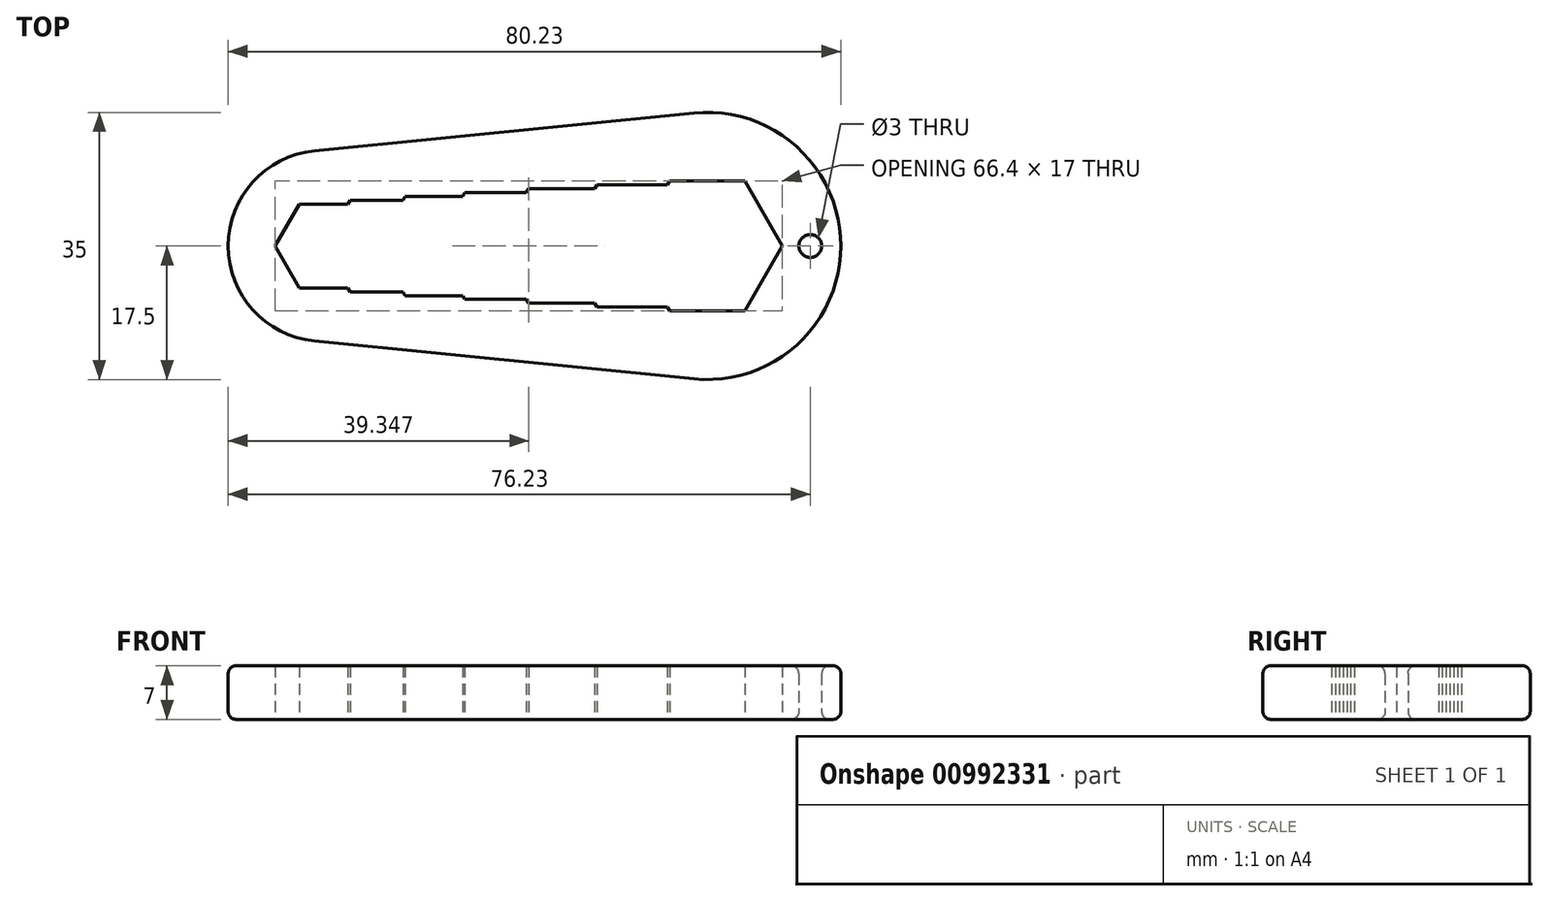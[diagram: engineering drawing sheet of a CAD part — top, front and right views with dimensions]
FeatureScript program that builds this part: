
annotation { "Feature Type Name" : "Feature", "Feature Type Description" : "" }
export const myFeature = defineFeature(function(context is Context, id is Id, definition is map)
    precondition{}
    {
        {
            var Q0;
            Q0=qCreatedBy(makeId("Top.planeOp"),FACE);
            var sketch = newSketch(context, id + "F0", { "sketchPlane" : qUnion([Q0])});
            skArc(sketch, "E0", {"start": v(-1.74, -17.41) * mm, "mid": v(17.5, 0) * mm, "end": v(-1.74, 17.41) * mm});
            skArc(sketch, "E1", {"start": v(-51.47, 12.44) * mm, "mid": v(-62.73, 0) * mm, "end": v(-51.47, -12.44) * mm});
            skLineSegment(sketch, "E2", {"start": v(-51.47, 12.44) * mm, "end": v(-1.74, 17.41) * mm});
            skLineSegment(sketch, "E3", {"start": v(-51.47, -12.44) * mm, "end": v(-1.74, -17.41) * mm});
            skCircle(sketch, "E4.cCircle", {"center": v(0, 0) * mm, "radius": 8.5 * mm, "construction": true});
            skLineSegment(sketch, "E4.0", {"start": v(9.81, 0) * mm, "end": v(4.9, -8.5) * mm});
            skLineSegment(sketch, "E4.1", {"start": v(4.9, -8.5) * mm, "end": v(-4.9, -8.5) * mm});
            skLineSegment(sketch, "E4.2", {"start": v(-4.9, -8.5) * mm, "end": v(-9.81, 0) * mm});
            skLineSegment(sketch, "E4.3", {"start": v(-9.81, 0) * mm, "end": v(-4.9, 8.5) * mm});
            skLineSegment(sketch, "E4.4", {"start": v(-4.9, 8.5) * mm, "end": v(4.9, 8.5) * mm});
            skLineSegment(sketch, "E4.5", {"start": v(4.9, 8.5) * mm, "end": v(9.81, 0) * mm});
            skPoint(sketch, "E4.0.midPoint", {"position": v(7.36, -4.25) * mm});
            skCircle(sketch, "E5.cCircle", {"center": v(-9.81, 0) * mm, "radius": 8 * mm, "construction": true});
            skLineSegment(sketch, "E5.0", {"start": v(-0.58, 0) * mm, "end": v(-5.2, -8) * mm});
            skLineSegment(sketch, "E5.1", {"start": v(-5.2, -8) * mm, "end": v(-14.43, -8) * mm});
            skLineSegment(sketch, "E5.2", {"start": v(-14.43, -8) * mm, "end": v(-19.05, 0) * mm});
            skLineSegment(sketch, "E5.3", {"start": v(-19.05, 0) * mm, "end": v(-14.43, 8) * mm});
            skLineSegment(sketch, "E5.4", {"start": v(-14.43, 8) * mm, "end": v(-5.2, 8) * mm});
            skLineSegment(sketch, "E5.5", {"start": v(-5.2, 8) * mm, "end": v(-0.58, 0) * mm});
            skPoint(sketch, "E5.0.midPoint", {"position": v(-2.89, -4) * mm});
            skCircle(sketch, "E6.cCircle", {"center": v(-19.05, 0) * mm, "radius": 7.5 * mm, "construction": true});
            skLineSegment(sketch, "E6.0", {"start": v(-10.4, 0) * mm, "end": v(-14.72, -7.5) * mm});
            skLineSegment(sketch, "E6.1", {"start": v(-14.72, -7.5) * mm, "end": v(-23.38, -7.5) * mm});
            skLineSegment(sketch, "E6.2", {"start": v(-23.38, -7.5) * mm, "end": v(-27.71, 0) * mm});
            skLineSegment(sketch, "E6.3", {"start": v(-27.71, 0) * mm, "end": v(-23.38, 7.5) * mm});
            skLineSegment(sketch, "E6.4", {"start": v(-23.38, 7.5) * mm, "end": v(-14.72, 7.5) * mm});
            skLineSegment(sketch, "E6.5", {"start": v(-14.72, 7.5) * mm, "end": v(-10.4, 0) * mm});
            skPoint(sketch, "E6.0.midPoint", {"position": v(-12.56, -3.75) * mm});
            skCircle(sketch, "E7.cCircle", {"center": v(-27.71, 0) * mm, "radius": 7 * mm, "construction": true});
            skLineSegment(sketch, "E7.0", {"start": v(-19.63, 0) * mm, "end": v(-23.67, -7) * mm});
            skLineSegment(sketch, "E7.1", {"start": v(-23.67, -7) * mm, "end": v(-31.75, -7) * mm});
            skLineSegment(sketch, "E7.2", {"start": v(-31.75, -7) * mm, "end": v(-35.8, 0) * mm});
            skLineSegment(sketch, "E7.3", {"start": v(-35.8, 0) * mm, "end": v(-31.75, 7) * mm});
            skLineSegment(sketch, "E7.4", {"start": v(-31.75, 7) * mm, "end": v(-23.67, 7) * mm});
            skLineSegment(sketch, "E7.5", {"start": v(-23.67, 7) * mm, "end": v(-19.63, 0) * mm});
            skPoint(sketch, "E7.0.midPoint", {"position": v(-21.65, -3.5) * mm});
            skCircle(sketch, "E8.cCircle", {"center": v(-35.8, 0) * mm, "radius": 6.5 * mm, "construction": true});
            skLineSegment(sketch, "E8.0", {"start": v(-28.3, 0) * mm, "end": v(-32.04, -6.5) * mm});
            skLineSegment(sketch, "E8.1", {"start": v(-32.04, -6.5) * mm, "end": v(-39.55, -6.5) * mm});
            skLineSegment(sketch, "E8.2", {"start": v(-39.55, -6.5) * mm, "end": v(-43.3, 0) * mm});
            skLineSegment(sketch, "E8.3", {"start": v(-43.3, 0) * mm, "end": v(-39.55, 6.5) * mm});
            skLineSegment(sketch, "E8.4", {"start": v(-39.55, 6.5) * mm, "end": v(-32.04, 6.5) * mm});
            skLineSegment(sketch, "E8.5", {"start": v(-32.04, 6.5) * mm, "end": v(-28.3, 0) * mm});
            skPoint(sketch, "E8.0.midPoint", {"position": v(-30.17, -3.25) * mm});
            skCircle(sketch, "E9.cCircle", {"center": v(-43.3, 0) * mm, "radius": 6 * mm, "construction": true});
            skLineSegment(sketch, "E9.0", {"start": v(-36.37, 0) * mm, "end": v(-39.84, -6) * mm});
            skLineSegment(sketch, "E9.1", {"start": v(-39.84, -6) * mm, "end": v(-46.77, -6) * mm});
            skLineSegment(sketch, "E9.2", {"start": v(-46.77, -6) * mm, "end": v(-50.23, 0) * mm});
            skLineSegment(sketch, "E9.3", {"start": v(-50.23, 0) * mm, "end": v(-46.77, 6) * mm});
            skLineSegment(sketch, "E9.4", {"start": v(-46.77, 6) * mm, "end": v(-39.84, 6) * mm});
            skLineSegment(sketch, "E9.5", {"start": v(-39.84, 6) * mm, "end": v(-36.37, 0) * mm});
            skPoint(sketch, "E9.0.midPoint", {"position": v(-38.1, -3) * mm});
            skCircle(sketch, "E10.cCircle", {"center": v(-50.23, 0) * mm, "radius": 5.5 * mm, "construction": true});
            skLineSegment(sketch, "E10.0", {"start": v(-43.88, 0) * mm, "end": v(-47.05, -5.5) * mm});
            skLineSegment(sketch, "E10.1", {"start": v(-47.05, -5.5) * mm, "end": v(-53.4, -5.5) * mm});
            skLineSegment(sketch, "E10.2", {"start": v(-53.4, -5.5) * mm, "end": v(-56.58, 0) * mm});
            skLineSegment(sketch, "E10.3", {"start": v(-56.58, 0) * mm, "end": v(-53.4, 5.5) * mm});
            skLineSegment(sketch, "E10.4", {"start": v(-53.4, 5.5) * mm, "end": v(-47.05, 5.5) * mm});
            skLineSegment(sketch, "E10.5", {"start": v(-47.05, 5.5) * mm, "end": v(-43.88, 0) * mm});
            skPoint(sketch, "E10.0.midPoint", {"position": v(-45.47, -2.75) * mm});
            skCircle(sketch, "E11", {"center": v(13.5, 0) * mm, "radius": 1.5 * mm});
            skPoint(sketch, "E12", {"position": v(17.5, 0) * mm});
            skSolve(sketch);
        }
        {
            var Q0;
            {var subQ7=sQuery(id+"F0.wireOp",EDGE,"E0");Q0=makeQuery(id+"F0.imprint","IMPRINT",FACE,{"disambiguationData":[TD([[makeQuery(id+"F0.imprint","IMPRINT",EDGE,{"derivedFrom":subQ7}),1.0]])]});}
            extrude(context, id + "F1", {"entities" : qUnion([Q0]), "depth" : 7 * mm, "offsetDistance" : 25 * mm});
        }
        {
            var Q0;
            Q0=makeQuery(id+"F1.opExtrude","CAP_EDGE",EDGE,{"disambiguationData":[OSD([sQuery(id+"F0.wireOp",EDGE,"E1")])],"isStart":false});
            var Q1;
            Q1=makeQuery(id+"F1.opExtrude","CAP_EDGE",EDGE,{"disambiguationData":[OSD([sQuery(id+"F0.wireOp",EDGE,"E3")])],"isStart":true});
            fillet(context, id + "F2", {"entities" : qUnion([Q0, Q1]), "radius" : 1 * mm, "tangentPropagation" : true, "allowEdgeOverflow" : false});
        }
        {
            var Q0;
            Q0=makeQuery(id+"F1.opExtrude","CAP_EDGE",EDGE,{"disambiguationData":[OSD([sQuery(id+"F0.wireOp",EDGE,"E11")])],"isStart":false});
            var Q1;
            Q1=makeQuery(id+"F1.opExtrude","CAP_EDGE",EDGE,{"disambiguationData":[OSD([sQuery(id+"F0.wireOp",EDGE,"E11")])],"isStart":true});
            fillet(context, id + "F3", {"entities" : qUnion([Q0, Q1]), "radius" : 1 * mm, "tangentPropagation" : true, "allowEdgeOverflow" : false});
        }
    });
